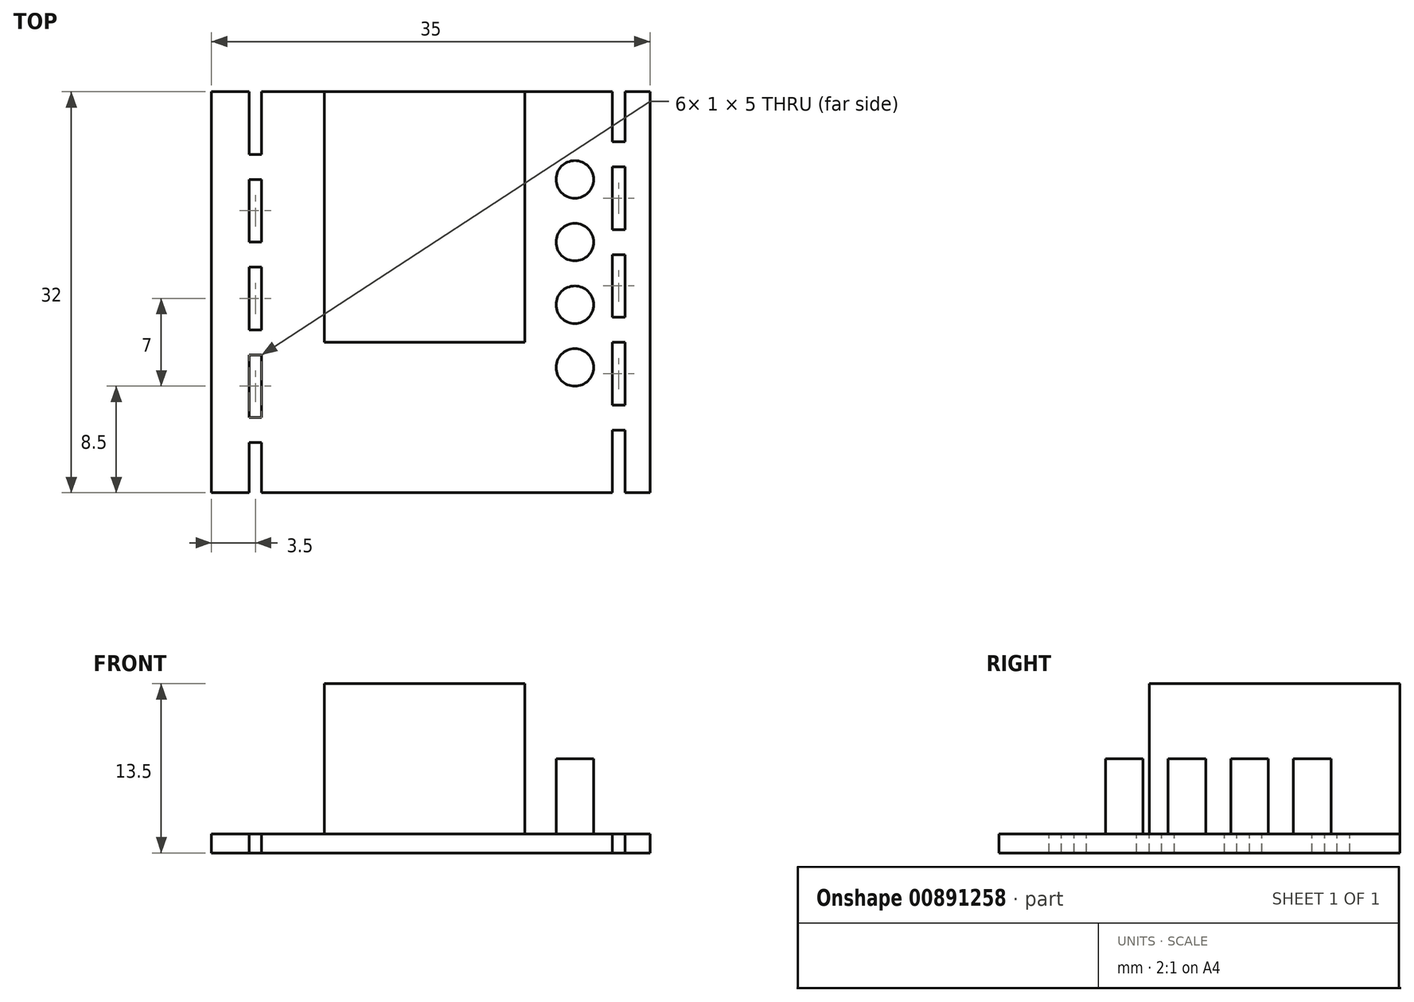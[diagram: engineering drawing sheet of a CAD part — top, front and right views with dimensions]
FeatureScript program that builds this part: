
annotation { "Feature Type Name" : "Feature", "Feature Type Description" : "" }
export const myFeature = defineFeature(function(context is Context, id is Id, definition is map)
    precondition{}
    {
        {
            var Q0;
            Q0=qCreatedBy(makeId("Top.planeOp"),FACE);
            var sketch = newSketch(context, id + "F0", { "sketchPlane" : qUnion([Q0])});
            skLineSegment(sketch, "E0.bottom", {"start": v(17.5, 16) * mm, "end": v(-17.5, 16) * mm});
            skLineSegment(sketch, "E0.top", {"start": v(17.5, -16) * mm, "end": v(-17.5, -16) * mm});
            skLineSegment(sketch, "E0.left", {"start": v(17.5, 16) * mm, "end": v(17.5, -16) * mm});
            skLineSegment(sketch, "E0.right", {"start": v(-17.5, 16) * mm, "end": v(-17.5, -16) * mm});
            skPoint(sketch, "E0.middle", {"position": v(0, 0) * mm});
            skSolve(sketch);
        }
        {
            var Q0;
            Q0=qSketchRegion(id+"F0",true);
            extrude(context, id + "F1", {"entities" : qUnion([Q0]), "depth" : 1.5 * mm, "offsetDistance" : 25 * mm});
        }
        {
            var Q0;
            Q0=makeQuery(id+"F1.opExtrude","CAP_FACE",FACE,{"disambiguationData":[OSD([sQuery(id+"F0.wireOp",EDGE,"E0.bottom"),sQuery(id+"F0.wireOp",EDGE,"E0.top"),sQuery(id+"F0.wireOp",EDGE,"E0.left"),sQuery(id+"F0.wireOp",EDGE,"E0.right")])],"isStart":false});
            var sketch = newSketch(context, id + "F2", { "sketchPlane" : qUnion([Q0])});
            skLineSegment(sketch, "E1.bottom", {"start": v(-8.5, 16) * mm, "end": v(7.5, 16) * mm});
            skLineSegment(sketch, "E1.top", {"start": v(-8.5, -4) * mm, "end": v(7.5, -4) * mm});
            skLineSegment(sketch, "E1.left", {"start": v(-8.5, 16) * mm, "end": v(-8.5, -4) * mm});
            skLineSegment(sketch, "E1.right", {"start": v(7.5, 16) * mm, "end": v(7.5, -4) * mm});
            skSolve(sketch);
        }
        {
            var Q0;
            Q0=qSketchRegion(id+"F2",true);
            extrude(context, id + "F3", {"entities" : qUnion([Q0]), "operationType" : NewBodyOperationType.ADD, "depth" : 12 * mm, "offsetDistance" : 25 * mm});
        }
        {
            var Q0;
            Q0=makeQuery(id+"F1.opExtrude","CAP_FACE",FACE,{"disambiguationData":[OSD([sQuery(id+"F0.wireOp",EDGE,"E0.bottom"),sQuery(id+"F0.wireOp",EDGE,"E0.top"),sQuery(id+"F0.wireOp",EDGE,"E0.left"),sQuery(id+"F0.wireOp",EDGE,"E0.right")])],"isStart":false});
            var sketch = newSketch(context, id + "F4", { "sketchPlane" : qUnion([Q0])});
            skCircle(sketch, "E2", {"center": v(11.5, 9) * mm, "radius": 1.5 * mm});
            skCircle(sketch, "E3.0.1.0", {"center": v(11.5, 4) * mm, "radius": 1.5 * mm});
            skCircle(sketch, "E3.0.2.0", {"center": v(11.5, -1) * mm, "radius": 1.5 * mm});
            skCircle(sketch, "E3.0.3.0", {"center": v(11.5, -6) * mm, "radius": 1.5 * mm});
            skLineSegment(sketch, "E3.direction1", {"start": v(11.5, 9) * mm, "end": v(36.5, 9) * mm, "construction": true});
            skLineSegment(sketch, "E3.direction2", {"start": v(11.5, 9) * mm, "end": v(11.5, 4) * mm, "construction": true});
            skSolve(sketch);
        }
        {
            var Q0;
            Q0=makeQuery(id+"F4.imprint","IMPRINT",FACE,{"disambiguationData":[TD([[makeQuery(id+"F4.imprint","IMPRINT",EDGE,{"derivedFrom":sQuery(id+"F4.wireOp",EDGE,"E2")}),1.0]])]});
            var Q1;
            Q1=makeQuery(id+"F4.imprint","IMPRINT",FACE,{"disambiguationData":[TD([[makeQuery(id+"F4.imprint","IMPRINT",EDGE,{"derivedFrom":sQuery(id+"F4.wireOp",EDGE,"E3.0.1.0")}),1.0]])]});
            var Q2;
            Q2=makeQuery(id+"F4.imprint","IMPRINT",FACE,{"disambiguationData":[TD([[makeQuery(id+"F4.imprint","IMPRINT",EDGE,{"derivedFrom":sQuery(id+"F4.wireOp",EDGE,"E3.0.2.0")}),1.0]])]});
            var Q3;
            Q3=makeQuery(id+"F4.imprint","IMPRINT",FACE,{"disambiguationData":[TD([[makeQuery(id+"F4.imprint","IMPRINT",EDGE,{"derivedFrom":sQuery(id+"F4.wireOp",EDGE,"E3.0.3.0")}),1.0]])]});
            extrude(context, id + "F5", {"entities" : qUnion([Q0, Q1, Q2, Q3]), "operationType" : NewBodyOperationType.ADD, "depth" : 6 * mm, "offsetDistance" : 25 * mm});
        }
        {
            var Q0;
            Q0=makeQuery(id+"F1.opExtrude","CAP_FACE",FACE,{"disambiguationData":[OSD([sQuery(id+"F0.wireOp",EDGE,"E0.bottom"),sQuery(id+"F0.wireOp",EDGE,"E0.top"),sQuery(id+"F0.wireOp",EDGE,"E0.left"),sQuery(id+"F0.wireOp",EDGE,"E0.right")])],"isStart":false});
            var sketch = newSketch(context, id + "F6", { "sketchPlane" : qUnion([Q0])});
            skLineSegment(sketch, "E4.bottom", {"start": v(-13.5, 16) * mm, "end": v(-14.5, 16) * mm});
            skLineSegment(sketch, "E4.top", {"start": v(-13.5, 11) * mm, "end": v(-14.5, 11) * mm});
            skLineSegment(sketch, "E4.left", {"start": v(-13.5, 16) * mm, "end": v(-13.5, 11) * mm});
            skLineSegment(sketch, "E4.right", {"start": v(-14.5, 16) * mm, "end": v(-14.5, 11) * mm});
            skLineSegment(sketch, "E5.0.1.0", {"start": v(-14.5, 9) * mm, "end": v(-14.5, 4) * mm});
            skLineSegment(sketch, "E5.0.1.1", {"start": v(-13.5, 4) * mm, "end": v(-14.5, 4) * mm});
            skLineSegment(sketch, "E5.0.1.2", {"start": v(-13.5, 9) * mm, "end": v(-13.5, 4) * mm});
            skLineSegment(sketch, "E5.0.1.3", {"start": v(-13.5, 9) * mm, "end": v(-14.5, 9) * mm});
            skLineSegment(sketch, "E5.0.2.0", {"start": v(-14.5, 2) * mm, "end": v(-14.5, -3) * mm});
            skLineSegment(sketch, "E5.0.2.1", {"start": v(-13.5, -3) * mm, "end": v(-14.5, -3) * mm});
            skLineSegment(sketch, "E5.0.2.2", {"start": v(-13.5, 2) * mm, "end": v(-13.5, -3) * mm});
            skLineSegment(sketch, "E5.0.2.3", {"start": v(-13.5, 2) * mm, "end": v(-14.5, 2) * mm});
            skLineSegment(sketch, "E5.0.3.0", {"start": v(-14.5, -5) * mm, "end": v(-14.5, -10) * mm});
            skLineSegment(sketch, "E5.0.3.1", {"start": v(-13.5, -10) * mm, "end": v(-14.5, -10) * mm});
            skLineSegment(sketch, "E5.0.3.2", {"start": v(-13.5, -5) * mm, "end": v(-13.5, -10) * mm});
            skLineSegment(sketch, "E5.0.3.3", {"start": v(-13.5, -5) * mm, "end": v(-14.5, -5) * mm});
            skLineSegment(sketch, "E5.0.4.0", {"start": v(-14.5, -12) * mm, "end": v(-14.5, -17) * mm});
            skLineSegment(sketch, "E5.0.4.1", {"start": v(-13.5, -17) * mm, "end": v(-14.5, -17) * mm});
            skLineSegment(sketch, "E5.0.4.2", {"start": v(-13.5, -12) * mm, "end": v(-13.5, -17) * mm});
            skLineSegment(sketch, "E5.0.4.3", {"start": v(-13.5, -12) * mm, "end": v(-14.5, -12) * mm});
            skLineSegment(sketch, "E5.direction1", {"start": v(-14.5, 11) * mm, "end": v(10.5, 11) * mm, "construction": true});
            skLineSegment(sketch, "E5.direction2", {"start": v(-14.5, 11) * mm, "end": v(-14.5, 4) * mm, "construction": true});
            skLineSegment(sketch, "E6.0.4.0", {"start": v(14.5, -11) * mm, "end": v(14.5, -16) * mm});
            skLineSegment(sketch, "E6.0.4.1", {"start": v(15.5, -16) * mm, "end": v(14.5, -16) * mm});
            skLineSegment(sketch, "E6.0.4.2", {"start": v(15.5, -11) * mm, "end": v(15.5, -16) * mm});
            skLineSegment(sketch, "E6.0.4.3", {"start": v(15.5, -11) * mm, "end": v(14.5, -11) * mm});
            skLineSegment(sketch, "E7.0.1.0", {"start": v(15.5, -4) * mm, "end": v(14.5, -4) * mm});
            skLineSegment(sketch, "E7.0.1.1", {"start": v(14.5, -4) * mm, "end": v(14.5, -9) * mm});
            skLineSegment(sketch, "E7.0.1.2", {"start": v(15.5, -4) * mm, "end": v(15.5, -9) * mm});
            skLineSegment(sketch, "E7.0.1.3", {"start": v(15.5, -9) * mm, "end": v(14.5, -9) * mm});
            skLineSegment(sketch, "E7.0.2.0", {"start": v(15.5, 3) * mm, "end": v(14.5, 3) * mm});
            skLineSegment(sketch, "E7.0.2.1", {"start": v(14.5, 3) * mm, "end": v(14.5, -2) * mm});
            skLineSegment(sketch, "E7.0.2.2", {"start": v(15.5, 3) * mm, "end": v(15.5, -2) * mm});
            skLineSegment(sketch, "E7.0.2.3", {"start": v(15.5, -2) * mm, "end": v(14.5, -2) * mm});
            skLineSegment(sketch, "E7.0.3.0", {"start": v(15.5, 10) * mm, "end": v(14.5, 10) * mm});
            skLineSegment(sketch, "E7.0.3.1", {"start": v(14.5, 10) * mm, "end": v(14.5, 5) * mm});
            skLineSegment(sketch, "E7.0.3.2", {"start": v(15.5, 10) * mm, "end": v(15.5, 5) * mm});
            skLineSegment(sketch, "E7.0.3.3", {"start": v(15.5, 5) * mm, "end": v(14.5, 5) * mm});
            skLineSegment(sketch, "E7.0.4.0", {"start": v(15.5, 17) * mm, "end": v(14.5, 17) * mm});
            skLineSegment(sketch, "E7.0.4.1", {"start": v(14.5, 17) * mm, "end": v(14.5, 12) * mm});
            skLineSegment(sketch, "E7.0.4.2", {"start": v(15.5, 17) * mm, "end": v(15.5, 12) * mm});
            skLineSegment(sketch, "E7.0.4.3", {"start": v(15.5, 12) * mm, "end": v(14.5, 12) * mm});
            skLineSegment(sketch, "E7.direction1", {"start": v(14.5, -16) * mm, "end": v(39.5, -16) * mm, "construction": true});
            skLineSegment(sketch, "E7.direction2", {"start": v(14.5, -16) * mm, "end": v(14.5, -9) * mm, "construction": true});
            skSolve(sketch);
        }
        {
            var Q0;
            Q0=qSketchRegion(id+"F6",true);
            var Q1;
            Q1=sQuery(id+"F6.wireOp",EDGE,"E6.0.4.2");
            var Q2;
            Q2=sQuery(id+"F6.wireOp",EDGE,"E6.0.4.0");
            var Q3;
            Q3=sQuery(id+"F6.wireOp",EDGE,"E6.0.4.1");
            var Q4;
            Q4=sQuery(id+"F6.wireOp",EDGE,"E6.0.4.3");
            extrude(context, id + "F7", {"entities" : qUnion([Q0]), "operationType" : NewBodyOperationType.REMOVE, "surfaceEntities" : qUnion([Q1, Q2, Q3, Q4]), "endBound" : BoundingType.UP_TO_NEXT, "oppositeDirection" : true, "depth" : 25 * mm, "offsetDistance" : 25 * mm});
        }
    });
